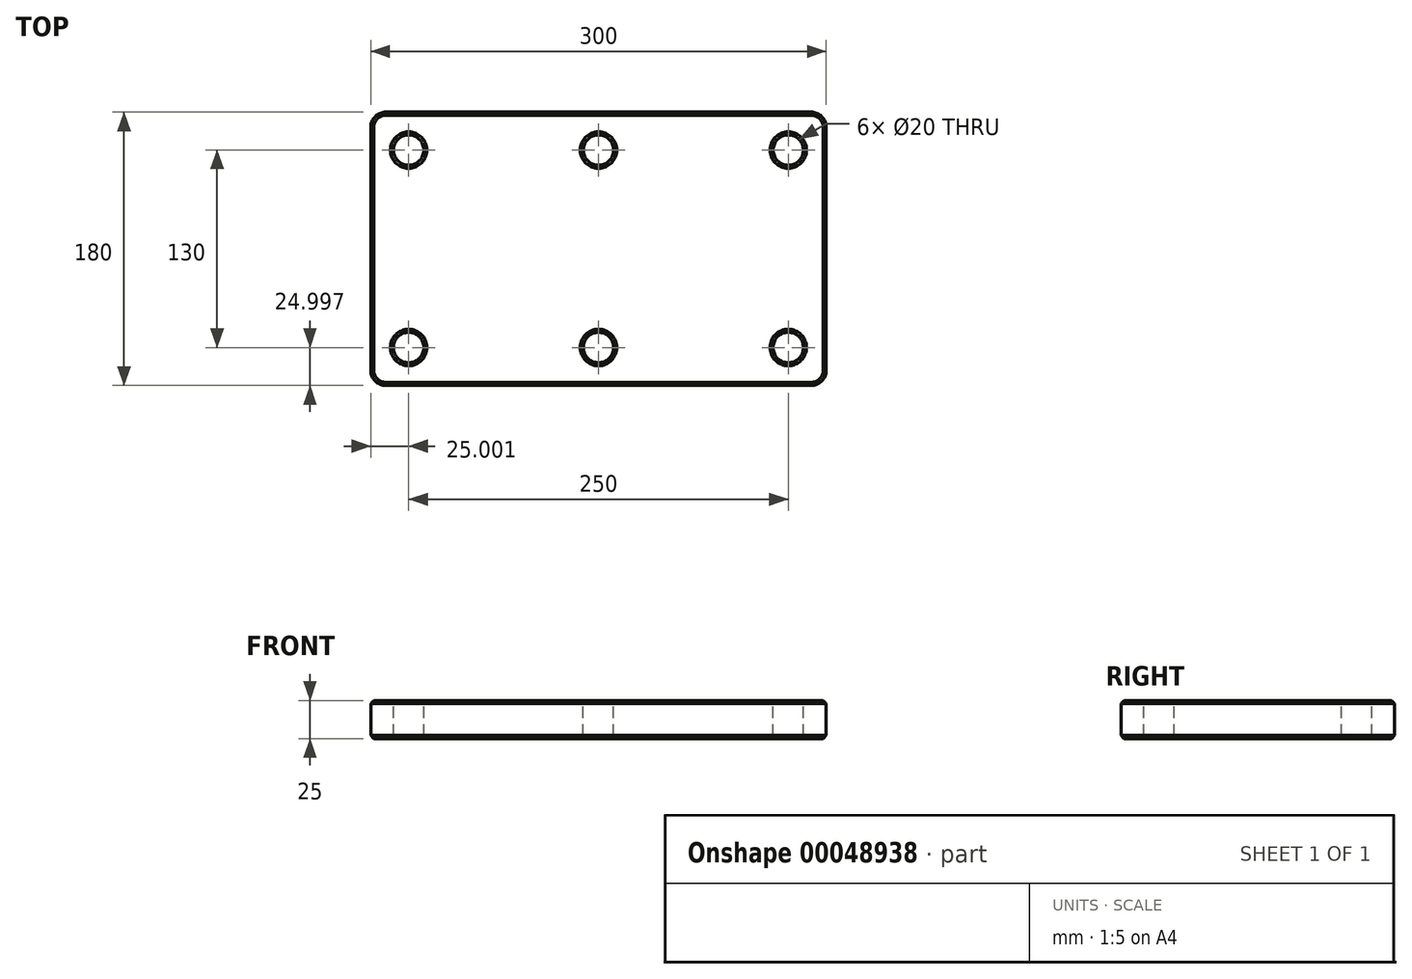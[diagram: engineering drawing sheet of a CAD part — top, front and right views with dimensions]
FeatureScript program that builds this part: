
annotation { "Feature Type Name" : "Feature", "Feature Type Description" : "" }
export const myFeature = defineFeature(function(context is Context, id is Id, definition is map)
    precondition{}
    {
        {
            var Q0;
            Q0=qCreatedBy(makeId("Top.planeOp"),FACE);
            var sketch = newSketch(context, id + "F0", { "sketchPlane" : qUnion([Q0])});
            skLineSegment(sketch, "E0.bottom", {"start": v(-170.04, 98.02) * mm, "end": v(129.96, 98.02) * mm});
            skLineSegment(sketch, "E0.top", {"start": v(-170.04, -81.98) * mm, "end": v(129.96, -81.98) * mm});
            skLineSegment(sketch, "E0.left", {"start": v(-170.04, 98.02) * mm, "end": v(-170.04, -81.98) * mm});
            skLineSegment(sketch, "E0.right", {"start": v(129.96, 98.02) * mm, "end": v(129.96, -81.98) * mm});
            skLineSegment(sketch, "E1", {"start": v(-170.04, 98.02) * mm, "end": v(-145.04, 98.02) * mm, "construction": true});
            skLineSegment(sketch, "E2", {"start": v(-145.04, 98.02) * mm, "end": v(-145.04, 73.02) * mm, "construction": true});
            skCircle(sketch, "E3", {"center": v(-145.04, 73.02) * mm, "radius": 10 * mm});
            skLineSegment(sketch, "E4", {"start": v(129.96, 98.02) * mm, "end": v(104.96, 98.02) * mm, "construction": true});
            skCircle(sketch, "E5", {"center": v(104.96, 73.02) * mm, "radius": 10 * mm});
            skLineSegment(sketch, "E6", {"start": v(-170.04, 98.02) * mm, "end": v(-170.04, 138.57) * mm, "construction": true});
            skCircle(sketch, "E7", {"center": v(-20.04, 73.02) * mm, "radius": 10 * mm});
            skCircle(sketch, "E8", {"center": v(-145.04, -56.98) * mm, "radius": 10 * mm});
            skCircle(sketch, "E9", {"center": v(104.96, -56.98) * mm, "radius": 10 * mm});
            skCircle(sketch, "E10", {"center": v(-20.04, -56.98) * mm, "radius": 10 * mm});
            skSolve(sketch);
        }
        {
            var Q0;
            Q0=makeQuery(id+"F0.imprint","IMPRINT",FACE,{"disambiguationData":[TD([[makeQuery(id+"F0.imprint","IMPRINT",EDGE,{"derivedFrom":sQuery(id+"F0.wireOp",EDGE,"E0.bottom")}),-1.0]])]});
            extrude(context, id + "F1", {"entities" : qUnion([Q0]), "oppositeDirection" : true, "depth" : 25 * mm});
        }
        {
            var Q0;
            Q0=makeQuery(id+"F1.opExtrude","CAP_EDGE",EDGE,{"disambiguationData":[OSD([sQuery(id+"F0.wireOp",EDGE,"E8")])],"isStart":true});
            var Q1;
            Q1=makeQuery(id+"F1.opExtrude","CAP_EDGE",EDGE,{"disambiguationData":[OSD([sQuery(id+"F0.wireOp",EDGE,"E3")])],"isStart":true});
            var Q2;
            Q2=makeQuery(id+"F1.opExtrude","CAP_EDGE",EDGE,{"disambiguationData":[OSD([sQuery(id+"F0.wireOp",EDGE,"E7")])],"isStart":true});
            var Q3;
            Q3=makeQuery(id+"F1.opExtrude","CAP_EDGE",EDGE,{"disambiguationData":[OSD([sQuery(id+"F0.wireOp",EDGE,"E10")])],"isStart":true});
            var Q4;
            Q4=makeQuery(id+"F1.opExtrude","CAP_EDGE",EDGE,{"disambiguationData":[OSD([sQuery(id+"F0.wireOp",EDGE,"E9")])],"isStart":true});
            var Q5;
            Q5=makeQuery(id+"F1.opExtrude","CAP_EDGE",EDGE,{"disambiguationData":[OSD([sQuery(id+"F0.wireOp",EDGE,"E5")])],"isStart":true});
            chamfer(context, id + "F2", {"entities" : qUnion([Q0, Q1, Q2, Q3, Q4, Q5]), "chamferType" : ChamferType.OFFSET_ANGLE, "width" : 2 * mm, "oppositeDirection" : false, "angle" : 45 * degree, "tangentPropagation" : true});
        }
        {
            var Q0;
            Q0=makeQuery(id+"F1.opExtrude","SWEPT_EDGE",EDGE,{"disambiguationData":[OSD([sQuery(id+"F0.wireOp",EDGE,"E0.top"),sQuery(id+"F0.wireOp",EDGE,"E0.right")])]});
            var Q1;
            Q1=makeQuery(id+"F1.opExtrude","SWEPT_EDGE",EDGE,{"disambiguationData":[OSD([sQuery(id+"F0.wireOp",EDGE,"E0.bottom"),sQuery(id+"F0.wireOp",EDGE,"E0.right")])]});
            var Q2;
            Q2=makeQuery(id+"F1.opExtrude","SWEPT_EDGE",EDGE,{"disambiguationData":[OSD([sQuery(id+"F0.wireOp",EDGE,"E0.top"),sQuery(id+"F0.wireOp",EDGE,"E0.left")])]});
            var Q3;
            Q3=makeQuery(id+"F1.opExtrude","SWEPT_EDGE",EDGE,{"disambiguationData":[OSD([sQuery(id+"F0.wireOp",EDGE,"E0.bottom"),sQuery(id+"F0.wireOp",EDGE,"E0.left")])]});
            fillet(context, id + "F3", {"entities" : qUnion([Q0, Q1, Q2, Q3]), "radius" : 10 * mm, "tangentPropagation" : true, "allowEdgeOverflow" : false});
        }
        {
            var Q0;
            {var subQ0=sQuery(id+"F0.wireOp",EDGE,"E0.top");var subQ1=sQuery(id+"F0.wireOp",EDGE,"E0.right");Q0=makeQuery(id+"F3.opFillet","BLEND_EDGE",EDGE,{"blendedFrom":[makeQuery(id+"F1.opExtrude","SWEPT_EDGE",EDGE,{"disambiguationData":[OSD([subQ0,subQ1])]}),makeQuery(id+"F1.opExtrude","CAP_FACE",FACE,{"disambiguationData":[OSD([sQuery(id+"F0.wireOp",EDGE,"E0.bottom"),subQ0,sQuery(id+"F0.wireOp",EDGE,"E0.left"),subQ1,sQuery(id+"F0.wireOp",EDGE,"E3"),sQuery(id+"F0.wireOp",EDGE,"E5"),sQuery(id+"F0.wireOp",EDGE,"E7"),sQuery(id+"F0.wireOp",EDGE,"E8"),sQuery(id+"F0.wireOp",EDGE,"E9"),sQuery(id+"F0.wireOp",EDGE,"E10")])],"isStart":false})],"blendedInto":[makeQuery(id+"F1.opExtrude","CAP_FACE",FACE,{"disambiguationData":[OSD([sQuery(id+"F0.wireOp",EDGE,"E0.bottom"),subQ0,sQuery(id+"F0.wireOp",EDGE,"E0.left"),subQ1,sQuery(id+"F0.wireOp",EDGE,"E3"),sQuery(id+"F0.wireOp",EDGE,"E5"),sQuery(id+"F0.wireOp",EDGE,"E7"),sQuery(id+"F0.wireOp",EDGE,"E8"),sQuery(id+"F0.wireOp",EDGE,"E9"),sQuery(id+"F0.wireOp",EDGE,"E10")])],"isStart":false})]});}
            var Q1;
            {var subQ0=sQuery(id+"F0.wireOp",EDGE,"E0.top");var subQ1=sQuery(id+"F0.wireOp",EDGE,"E0.left");Q1=makeQuery(id+"F3.opFillet","BLEND_EDGE",EDGE,{"blendedFrom":[makeQuery(id+"F1.opExtrude","SWEPT_EDGE",EDGE,{"disambiguationData":[OSD([subQ0,subQ1])]}),makeQuery(id+"F1.opExtrude","CAP_FACE",FACE,{"disambiguationData":[OSD([sQuery(id+"F0.wireOp",EDGE,"E0.bottom"),subQ0,subQ1,sQuery(id+"F0.wireOp",EDGE,"E0.right"),sQuery(id+"F0.wireOp",EDGE,"E3"),sQuery(id+"F0.wireOp",EDGE,"E5"),sQuery(id+"F0.wireOp",EDGE,"E7"),sQuery(id+"F0.wireOp",EDGE,"E8"),sQuery(id+"F0.wireOp",EDGE,"E9"),sQuery(id+"F0.wireOp",EDGE,"E10")])],"isStart":false})],"blendedInto":[makeQuery(id+"F1.opExtrude","CAP_FACE",FACE,{"disambiguationData":[OSD([sQuery(id+"F0.wireOp",EDGE,"E0.bottom"),subQ0,subQ1,sQuery(id+"F0.wireOp",EDGE,"E0.right"),sQuery(id+"F0.wireOp",EDGE,"E3"),sQuery(id+"F0.wireOp",EDGE,"E5"),sQuery(id+"F0.wireOp",EDGE,"E7"),sQuery(id+"F0.wireOp",EDGE,"E8"),sQuery(id+"F0.wireOp",EDGE,"E9"),sQuery(id+"F0.wireOp",EDGE,"E10")])],"isStart":false})]});}
            var Q2;
            {var subQ0=sQuery(id+"F0.wireOp",EDGE,"E0.bottom");var subQ1=sQuery(id+"F0.wireOp",EDGE,"E0.left");Q2=makeQuery(id+"F3.opFillet","BLEND_EDGE",EDGE,{"blendedFrom":[makeQuery(id+"F1.opExtrude","SWEPT_EDGE",EDGE,{"disambiguationData":[OSD([subQ0,subQ1])]}),makeQuery(id+"F1.opExtrude","CAP_FACE",FACE,{"disambiguationData":[OSD([subQ0,sQuery(id+"F0.wireOp",EDGE,"E0.top"),subQ1,sQuery(id+"F0.wireOp",EDGE,"E0.right"),sQuery(id+"F0.wireOp",EDGE,"E3"),sQuery(id+"F0.wireOp",EDGE,"E5"),sQuery(id+"F0.wireOp",EDGE,"E7"),sQuery(id+"F0.wireOp",EDGE,"E8"),sQuery(id+"F0.wireOp",EDGE,"E9"),sQuery(id+"F0.wireOp",EDGE,"E10")])],"isStart":false})],"blendedInto":[makeQuery(id+"F1.opExtrude","CAP_FACE",FACE,{"disambiguationData":[OSD([subQ0,sQuery(id+"F0.wireOp",EDGE,"E0.top"),subQ1,sQuery(id+"F0.wireOp",EDGE,"E0.right"),sQuery(id+"F0.wireOp",EDGE,"E3"),sQuery(id+"F0.wireOp",EDGE,"E5"),sQuery(id+"F0.wireOp",EDGE,"E7"),sQuery(id+"F0.wireOp",EDGE,"E8"),sQuery(id+"F0.wireOp",EDGE,"E9"),sQuery(id+"F0.wireOp",EDGE,"E10")])],"isStart":false})]});}
            var Q3;
            {var subQ0=sQuery(id+"F0.wireOp",EDGE,"E0.bottom");var subQ1=sQuery(id+"F0.wireOp",EDGE,"E0.right");Q3=makeQuery(id+"F3.opFillet","BLEND_EDGE",EDGE,{"blendedFrom":[makeQuery(id+"F1.opExtrude","SWEPT_EDGE",EDGE,{"disambiguationData":[OSD([subQ0,subQ1])]}),makeQuery(id+"F1.opExtrude","CAP_FACE",FACE,{"disambiguationData":[OSD([subQ0,sQuery(id+"F0.wireOp",EDGE,"E0.top"),sQuery(id+"F0.wireOp",EDGE,"E0.left"),subQ1,sQuery(id+"F0.wireOp",EDGE,"E3"),sQuery(id+"F0.wireOp",EDGE,"E5"),sQuery(id+"F0.wireOp",EDGE,"E7"),sQuery(id+"F0.wireOp",EDGE,"E8"),sQuery(id+"F0.wireOp",EDGE,"E9"),sQuery(id+"F0.wireOp",EDGE,"E10")])],"isStart":false})],"blendedInto":[makeQuery(id+"F1.opExtrude","CAP_FACE",FACE,{"disambiguationData":[OSD([subQ0,sQuery(id+"F0.wireOp",EDGE,"E0.top"),sQuery(id+"F0.wireOp",EDGE,"E0.left"),subQ1,sQuery(id+"F0.wireOp",EDGE,"E3"),sQuery(id+"F0.wireOp",EDGE,"E5"),sQuery(id+"F0.wireOp",EDGE,"E7"),sQuery(id+"F0.wireOp",EDGE,"E8"),sQuery(id+"F0.wireOp",EDGE,"E9"),sQuery(id+"F0.wireOp",EDGE,"E10")])],"isStart":false})]});}
            chamfer(context, id + "F4", {"entities" : qUnion([Q0, Q1, Q2, Q3]), "chamferType" : ChamferType.OFFSET_ANGLE, "width" : 2 * mm, "oppositeDirection" : false, "angle" : 45 * degree, "tangentPropagation" : true});
        }
        {
            var Q0;
            {var subQ0=sQuery(id+"F0.wireOp",EDGE,"E0.bottom");var subQ1=sQuery(id+"F0.wireOp",EDGE,"E0.left");Q0=makeQuery(id+"F3.opFillet","BLEND_EDGE",EDGE,{"blendedFrom":[makeQuery(id+"F1.opExtrude","SWEPT_EDGE",EDGE,{"disambiguationData":[OSD([subQ0,subQ1])]}),makeQuery(id+"F1.opExtrude","CAP_FACE",FACE,{"disambiguationData":[OSD([subQ0,sQuery(id+"F0.wireOp",EDGE,"E0.top"),subQ1,sQuery(id+"F0.wireOp",EDGE,"E0.right"),sQuery(id+"F0.wireOp",EDGE,"E3"),sQuery(id+"F0.wireOp",EDGE,"E5"),sQuery(id+"F0.wireOp",EDGE,"E7"),sQuery(id+"F0.wireOp",EDGE,"E8"),sQuery(id+"F0.wireOp",EDGE,"E9"),sQuery(id+"F0.wireOp",EDGE,"E10")])],"isStart":true})],"blendedInto":[makeQuery(id+"F1.opExtrude","CAP_FACE",FACE,{"disambiguationData":[OSD([subQ0,sQuery(id+"F0.wireOp",EDGE,"E0.top"),subQ1,sQuery(id+"F0.wireOp",EDGE,"E0.right"),sQuery(id+"F0.wireOp",EDGE,"E3"),sQuery(id+"F0.wireOp",EDGE,"E5"),sQuery(id+"F0.wireOp",EDGE,"E7"),sQuery(id+"F0.wireOp",EDGE,"E8"),sQuery(id+"F0.wireOp",EDGE,"E9"),sQuery(id+"F0.wireOp",EDGE,"E10")])],"isStart":true})]});}
            var Q1;
            {var subQ0=sQuery(id+"F0.wireOp",EDGE,"E0.top");var subQ1=sQuery(id+"F0.wireOp",EDGE,"E0.left");Q1=makeQuery(id+"F3.opFillet","BLEND_EDGE",EDGE,{"blendedFrom":[makeQuery(id+"F1.opExtrude","SWEPT_EDGE",EDGE,{"disambiguationData":[OSD([subQ0,subQ1])]}),makeQuery(id+"F1.opExtrude","CAP_FACE",FACE,{"disambiguationData":[OSD([sQuery(id+"F0.wireOp",EDGE,"E0.bottom"),subQ0,subQ1,sQuery(id+"F0.wireOp",EDGE,"E0.right"),sQuery(id+"F0.wireOp",EDGE,"E3"),sQuery(id+"F0.wireOp",EDGE,"E5"),sQuery(id+"F0.wireOp",EDGE,"E7"),sQuery(id+"F0.wireOp",EDGE,"E8"),sQuery(id+"F0.wireOp",EDGE,"E9"),sQuery(id+"F0.wireOp",EDGE,"E10")])],"isStart":true})],"blendedInto":[makeQuery(id+"F1.opExtrude","CAP_FACE",FACE,{"disambiguationData":[OSD([sQuery(id+"F0.wireOp",EDGE,"E0.bottom"),subQ0,subQ1,sQuery(id+"F0.wireOp",EDGE,"E0.right"),sQuery(id+"F0.wireOp",EDGE,"E3"),sQuery(id+"F0.wireOp",EDGE,"E5"),sQuery(id+"F0.wireOp",EDGE,"E7"),sQuery(id+"F0.wireOp",EDGE,"E8"),sQuery(id+"F0.wireOp",EDGE,"E9"),sQuery(id+"F0.wireOp",EDGE,"E10")])],"isStart":true})]});}
            var Q2;
            {var subQ0=sQuery(id+"F0.wireOp",EDGE,"E0.bottom");var subQ1=sQuery(id+"F0.wireOp",EDGE,"E0.right");Q2=makeQuery(id+"F3.opFillet","BLEND_EDGE",EDGE,{"blendedFrom":[makeQuery(id+"F1.opExtrude","SWEPT_EDGE",EDGE,{"disambiguationData":[OSD([subQ0,subQ1])]}),makeQuery(id+"F1.opExtrude","CAP_FACE",FACE,{"disambiguationData":[OSD([subQ0,sQuery(id+"F0.wireOp",EDGE,"E0.top"),sQuery(id+"F0.wireOp",EDGE,"E0.left"),subQ1,sQuery(id+"F0.wireOp",EDGE,"E3"),sQuery(id+"F0.wireOp",EDGE,"E5"),sQuery(id+"F0.wireOp",EDGE,"E7"),sQuery(id+"F0.wireOp",EDGE,"E8"),sQuery(id+"F0.wireOp",EDGE,"E9"),sQuery(id+"F0.wireOp",EDGE,"E10")])],"isStart":true})],"blendedInto":[makeQuery(id+"F1.opExtrude","CAP_FACE",FACE,{"disambiguationData":[OSD([subQ0,sQuery(id+"F0.wireOp",EDGE,"E0.top"),sQuery(id+"F0.wireOp",EDGE,"E0.left"),subQ1,sQuery(id+"F0.wireOp",EDGE,"E3"),sQuery(id+"F0.wireOp",EDGE,"E5"),sQuery(id+"F0.wireOp",EDGE,"E7"),sQuery(id+"F0.wireOp",EDGE,"E8"),sQuery(id+"F0.wireOp",EDGE,"E9"),sQuery(id+"F0.wireOp",EDGE,"E10")])],"isStart":true})]});}
            var Q3;
            {var subQ0=sQuery(id+"F0.wireOp",EDGE,"E0.top");var subQ1=sQuery(id+"F0.wireOp",EDGE,"E0.right");Q3=makeQuery(id+"F3.opFillet","BLEND_EDGE",EDGE,{"blendedFrom":[makeQuery(id+"F1.opExtrude","SWEPT_EDGE",EDGE,{"disambiguationData":[OSD([subQ0,subQ1])]}),makeQuery(id+"F1.opExtrude","CAP_FACE",FACE,{"disambiguationData":[OSD([sQuery(id+"F0.wireOp",EDGE,"E0.bottom"),subQ0,sQuery(id+"F0.wireOp",EDGE,"E0.left"),subQ1,sQuery(id+"F0.wireOp",EDGE,"E3"),sQuery(id+"F0.wireOp",EDGE,"E5"),sQuery(id+"F0.wireOp",EDGE,"E7"),sQuery(id+"F0.wireOp",EDGE,"E8"),sQuery(id+"F0.wireOp",EDGE,"E9"),sQuery(id+"F0.wireOp",EDGE,"E10")])],"isStart":true})],"blendedInto":[makeQuery(id+"F1.opExtrude","CAP_FACE",FACE,{"disambiguationData":[OSD([sQuery(id+"F0.wireOp",EDGE,"E0.bottom"),subQ0,sQuery(id+"F0.wireOp",EDGE,"E0.left"),subQ1,sQuery(id+"F0.wireOp",EDGE,"E3"),sQuery(id+"F0.wireOp",EDGE,"E5"),sQuery(id+"F0.wireOp",EDGE,"E7"),sQuery(id+"F0.wireOp",EDGE,"E8"),sQuery(id+"F0.wireOp",EDGE,"E9"),sQuery(id+"F0.wireOp",EDGE,"E10")])],"isStart":true})]});}
            chamfer(context, id + "F5", {"entities" : qUnion([Q0, Q1, Q2, Q3]), "chamferType" : ChamferType.OFFSET_ANGLE, "width" : 2 * mm, "oppositeDirection" : false, "angle" : 45 * degree, "tangentPropagation" : true});
        }
        {
            var Q0;
            Q0=makeQuery(id+"F1.opExtrude","CAP_EDGE",EDGE,{"disambiguationData":[OSD([sQuery(id+"F0.wireOp",EDGE,"E5")])],"isStart":false});
            var Q1;
            Q1=makeQuery(id+"F1.opExtrude","CAP_EDGE",EDGE,{"disambiguationData":[OSD([sQuery(id+"F0.wireOp",EDGE,"E7")])],"isStart":false});
            var Q2;
            Q2=makeQuery(id+"F1.opExtrude","CAP_EDGE",EDGE,{"disambiguationData":[OSD([sQuery(id+"F0.wireOp",EDGE,"E9")])],"isStart":false});
            var Q3;
            Q3=makeQuery(id+"F1.opExtrude","CAP_EDGE",EDGE,{"disambiguationData":[OSD([sQuery(id+"F0.wireOp",EDGE,"E10")])],"isStart":false});
            var Q4;
            Q4=makeQuery(id+"F1.opExtrude","CAP_EDGE",EDGE,{"disambiguationData":[OSD([sQuery(id+"F0.wireOp",EDGE,"E8")])],"isStart":false});
            var Q5;
            Q5=makeQuery(id+"F1.opExtrude","CAP_EDGE",EDGE,{"disambiguationData":[OSD([sQuery(id+"F0.wireOp",EDGE,"E3")])],"isStart":false});
            chamfer(context, id + "F6", {"entities" : qUnion([Q0, Q1, Q2, Q3, Q4, Q5]), "chamferType" : ChamferType.OFFSET_ANGLE, "width" : 2 * mm, "oppositeDirection" : false, "angle" : 45 * degree, "tangentPropagation" : true});
        }
    });
